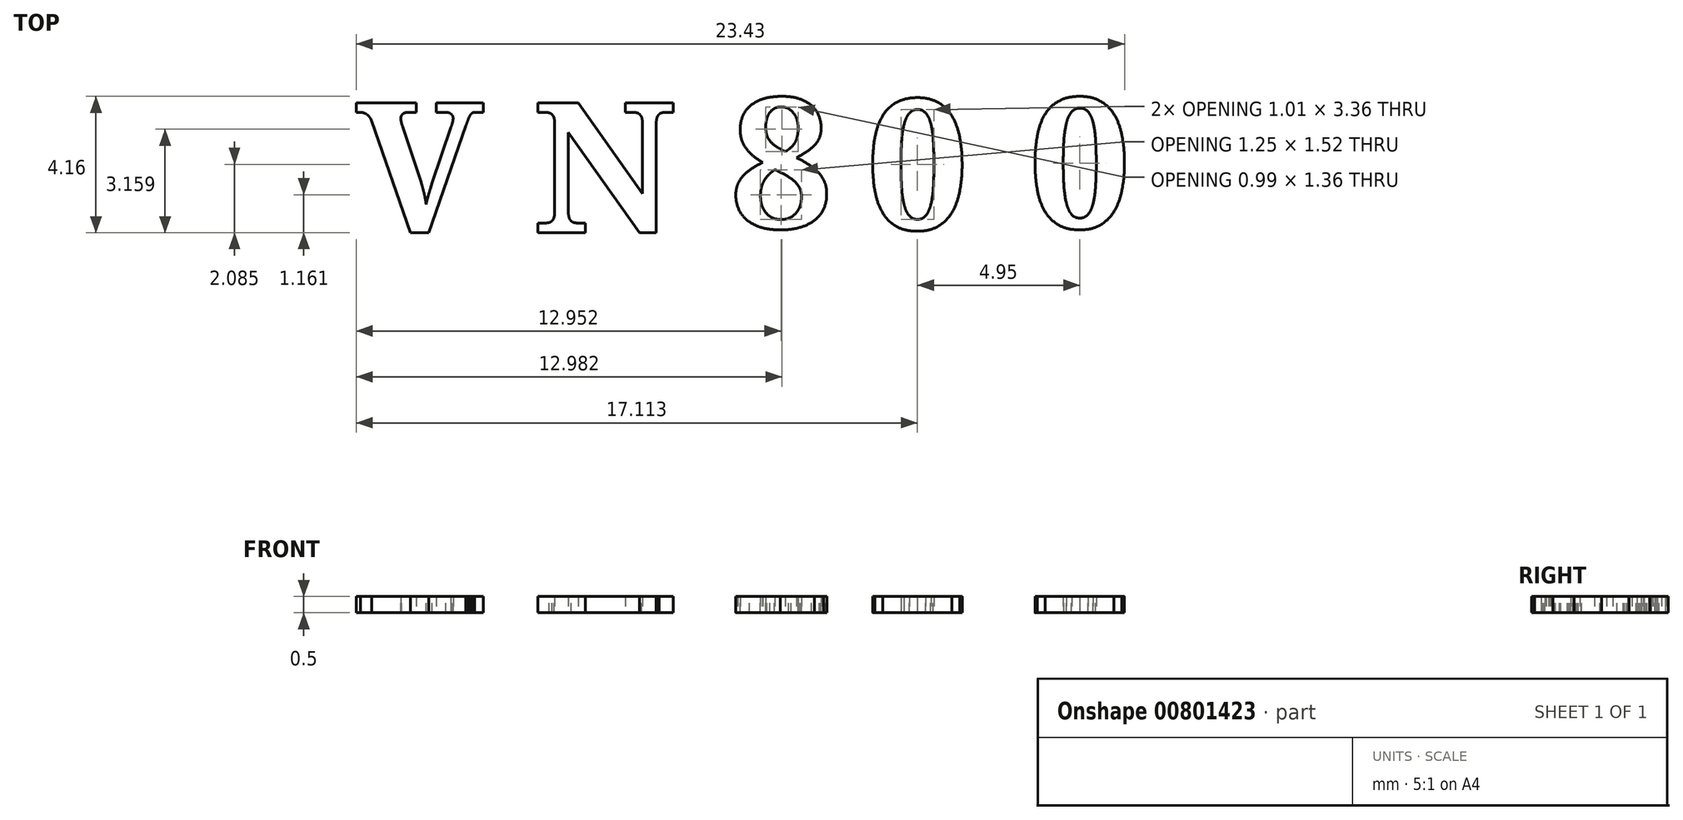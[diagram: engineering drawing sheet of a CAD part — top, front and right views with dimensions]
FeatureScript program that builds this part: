
annotation { "Feature Type Name" : "Feature", "Feature Type Description" : "" }
export const myFeature = defineFeature(function(context is Context, id is Id, definition is map)
    precondition{}
    {
        {
            var Q0;
            Q0=qCreatedBy(makeId("Top.planeOp"),FACE);
            var sketch = newSketch(context, id + "F0", { "sketchPlane" : qUnion([Q0])});
            skText(sketch, "E0", { "text": "V", "fontName": "NotoSerif-Bold.ttf"});
            skText(sketch, "E1", { "text": "N", "fontName": "NotoSerif-Bold.ttf"});
            skText(sketch, "E2", { "text": "8", "fontName": "NotoSerif-Bold.ttf"});
            skText(sketch, "E3", { "text": "0", "fontName": "NotoSerif-Bold.ttf"});
            skText(sketch, "E4", { "text": "0", "fontName": "NotoSerif-Bold.ttf"});
            const initialGuessF0  = {"E0": [-0.01218, 0.00593, 1, 0, 0.004], "E1": [-0.0068, 0.00593, 1, 0, 0.004], "E2": [-0.00077, 0.00607, 1, 0, 0.004], "E3": [0.00338, 0.00603, 1, 0, 0.004], "E4": [0.00833, 0.00607, 1, 0, 0.004]};
            skSetInitialGuess(sketch, initialGuessF0);
            skSolve(sketch);
        }
        {
            var Q0;
            Q0 = qSketchRegion(id + "F0", true);
            extrude(context, id + "F1", {"entities" : qUnion([Q0]), "depth" : 0.5 * mm, "offsetDistance" : 25 * mm});
        }
    });
